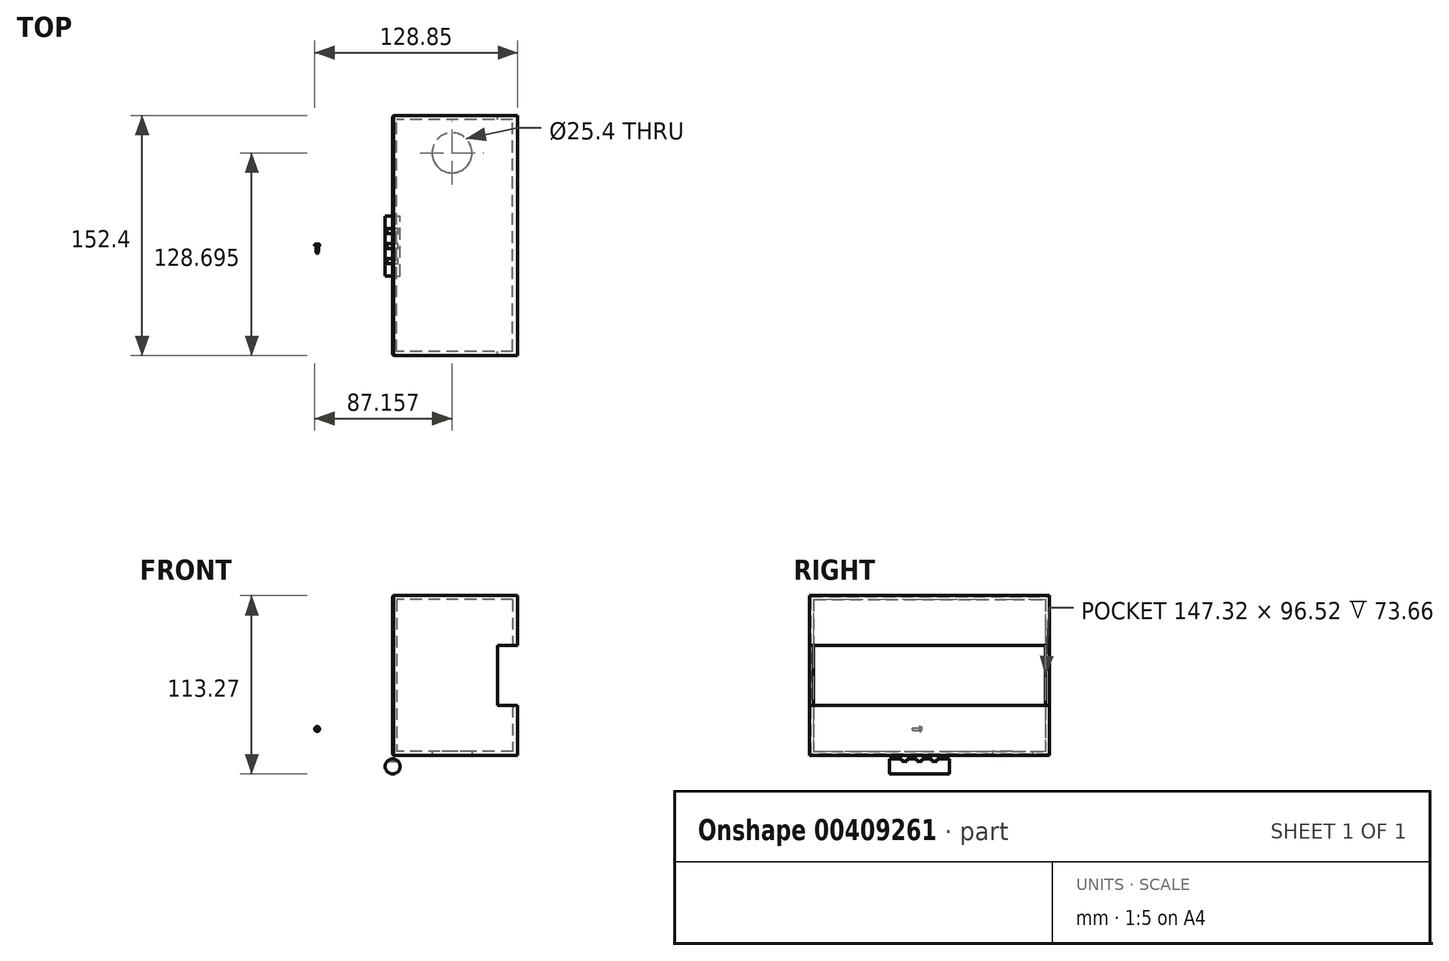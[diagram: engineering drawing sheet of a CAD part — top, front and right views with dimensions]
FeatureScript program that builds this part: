
annotation { "Feature Type Name" : "Feature", "Feature Type Description" : "" }
export const myFeature = defineFeature(function(context is Context, id is Id, definition is map)
    precondition{}
    {
        {
            var Q0;
            Q0=qCreatedBy(makeId("Front.planeOp"),FACE);
            var sketch = newSketch(context, id + "F0", { "sketchPlane" : qUnion([Q0])});
            skCircle(sketch, "E0", {"center": v(0, 0) * mm, "radius": 4.76 * mm});
            skSolve(sketch);
        }
        {
            var Q0;
            Q0=qSketchRegion(id+"F0",true);
            extrude(context, id + "F1", {"entities" : qUnion([Q0]), "endBound" : BoundingType.SYMMETRIC, "depth" : 38.1 * mm});
        }
        {
            var Q0;
            Q0=qCreatedBy(makeId("Right.planeOp"),FACE);
            var sketch = newSketch(context, id + "F2", { "sketchPlane" : qUnion([Q0])});
            skLineSegment(sketch, "E1.bottom", {"start": v(-1.59, 6.48) * mm, "end": v(1.59, 6.48) * mm});
            skLineSegment(sketch, "E1.top", {"start": v(-1.59, 3.18) * mm, "end": v(1.59, 3.18) * mm});
            skLineSegment(sketch, "E1.left", {"start": v(-1.59, 6.48) * mm, "end": v(-1.59, 3.18) * mm});
            skLineSegment(sketch, "E1.right", {"start": v(1.59, 6.48) * mm, "end": v(1.59, 3.18) * mm});
            skLineSegment(sketch, "E2.bottom", {"start": v(7.94, 6.48) * mm, "end": v(11.11, 6.48) * mm});
            skLineSegment(sketch, "E2.top", {"start": v(7.94, 3.17) * mm, "end": v(11.11, 3.18) * mm});
            skLineSegment(sketch, "E2.left", {"start": v(7.94, 6.48) * mm, "end": v(7.94, 3.17) * mm});
            skLineSegment(sketch, "E2.right", {"start": v(11.11, 6.48) * mm, "end": v(11.11, 3.18) * mm});
            skLineSegment(sketch, "E3.MirrorCS", {"start": v(-7.94, 6.48) * mm, "end": v(-11.11, 6.48) * mm});
            skLineSegment(sketch, "E4.MirrorCS", {"start": v(-11.11, 6.48) * mm, "end": v(-11.11, 3.18) * mm});
            skLineSegment(sketch, "E5.MirrorCS", {"start": v(-7.94, 3.17) * mm, "end": v(-11.11, 3.18) * mm});
            skLineSegment(sketch, "E6.MirrorCS", {"start": v(-7.94, 6.48) * mm, "end": v(-7.94, 3.17) * mm});
            skSolve(sketch);
        }
        {
            var Q0;
            Q0=qSketchRegion(id+"F2",true);
            extrude(context, id + "F3", {"entities" : qUnion([Q0]), "operationType" : NewBodyOperationType.REMOVE, "endBound" : BoundingType.SYMMETRIC, "oppositeDirection" : true, "depth" : 25.4 * mm});
        }
        {
            var Q0;
            Q0=qCreatedBy(makeId("Right.planeOp"),FACE);
            var sketch = newSketch(context, id + "F4", { "sketchPlane" : qUnion([Q0])});
            skLineSegment(sketch, "E7.bottom", {"start": v(-69.66, 108.51) * mm, "end": v(82.74, 108.51) * mm});
            skLineSegment(sketch, "E7.top", {"start": v(-69.66, 6.91) * mm, "end": v(82.74, 6.91) * mm});
            skLineSegment(sketch, "E7.left", {"start": v(-69.66, 108.51) * mm, "end": v(-69.66, 6.91) * mm});
            skLineSegment(sketch, "E7.right", {"start": v(82.74, 108.51) * mm, "end": v(82.74, 6.91) * mm});
            skSolve(sketch);
        }
        {
            var Q0;
            Q0=qSketchRegion(id+"F4",true);
            extrude(context, id + "F5", {"entities" : qUnion([Q0]), "depth" : 76.2 * mm});
        }
        {
            var Q0;
            Q0=makeQuery(id+"F5.opExtrude","CAP_FACE",FACE,{"disambiguationData":[OSD([sQuery(id+"F4.wireOp",EDGE,"E7.bottom"),sQuery(id+"F4.wireOp",EDGE,"E7.top"),sQuery(id+"F4.wireOp",EDGE,"E7.left"),sQuery(id+"F4.wireOp",EDGE,"E7.right")])],"isStart":false});
            shell(context, id + "F6", {"entities" : qUnion([Q0]), "thickness" : 2.54 * mm});
        }
        {
            var Q0;
            Q0=makeQuery(id+"F5.opExtrude","CAP_FACE",FACE,{"disambiguationData":[OSD([sQuery(id+"F4.wireOp",EDGE,"E7.bottom"),sQuery(id+"F4.wireOp",EDGE,"E7.top"),sQuery(id+"F4.wireOp",EDGE,"E7.left"),sQuery(id+"F4.wireOp",EDGE,"E7.right")])],"isStart":false});
            var sketch = newSketch(context, id + "F7", { "sketchPlane" : qUnion([Q0])});
            skLineSegment(sketch, "E8.bottom", {"start": v(-69.66, 108.51) * mm, "end": v(82.74, 108.51) * mm});
            skLineSegment(sketch, "E8.top", {"start": v(-69.66, 6.91) * mm, "end": v(82.74, 6.91) * mm});
            skLineSegment(sketch, "E8.left", {"start": v(-69.66, 108.51) * mm, "end": v(-69.66, 6.91) * mm});
            skLineSegment(sketch, "E8.right", {"start": v(82.74, 108.51) * mm, "end": v(82.74, 6.91) * mm});
            skSolve(sketch);
        }
        {
            var Q0;
            Q0=qSketchRegion(id+"F7",true);
            extrude(context, id + "F8", {"entities" : qUnion([Q0]), "operationType" : NewBodyOperationType.ADD, "depth" : 3.17 * mm});
        }
        {
            var Q0;
            Q0=makeQuery(id+"F8.opExtrude","CAP_FACE",FACE,{"disambiguationData":[OSD([sQuery(id+"F7.wireOp",EDGE,"E8.bottom"),sQuery(id+"F7.wireOp",EDGE,"E8.top"),sQuery(id+"F7.wireOp",EDGE,"E8.left"),sQuery(id+"F7.wireOp",EDGE,"E8.right")])],"isStart":false});
            var sketch = newSketch(context, id + "F9", { "sketchPlane" : qUnion([Q0])});
            skLineSegment(sketch, "E9.bottom", {"start": v(-82.06, 76.76) * mm, "end": v(95.74, 76.76) * mm});
            skLineSegment(sketch, "E9.top", {"start": v(-82.06, 38.66) * mm, "end": v(95.74, 38.66) * mm});
            skLineSegment(sketch, "E9.left", {"start": v(-82.06, 76.76) * mm, "end": v(-82.06, 38.66) * mm});
            skLineSegment(sketch, "E9.right", {"start": v(95.74, 76.76) * mm, "end": v(95.74, 38.66) * mm});
            skLineSegment(sketch, "E10", {"start": v(-69.66, 57.71) * mm, "end": v(82.74, 57.71) * mm, "construction": true});
            skSolve(sketch);
        }
        {
            var Q0;
            Q0=qSketchRegion(id+"F9",true);
            extrude(context, id + "F10", {"entities" : qUnion([Q0]), "operationType" : NewBodyOperationType.REMOVE, "oppositeDirection" : true, "depth" : 12.7 * mm});
        }
        {
            var Q0;
            Q0=makeQuery(id+"F8.boolean.opBoolean","MERGE",FACE,{"derivedFrom":[makeQuery(id+"F5.opExtrude","SWEPT_FACE",FACE,{"disambiguationData":[OSD([sQuery(id+"F4.wireOp",EDGE,"E7.top")])]}),makeQuery(id+"F8.opExtrude","SWEPT_FACE",FACE,{"disambiguationData":[OSD([sQuery(id+"F7.wireOp",EDGE,"E8.top")])]})]});
            var sketch = newSketch(context, id + "F11", { "sketchPlane" : qUnion([Q0])});
            skCircle(sketch, "E11", {"center": v(37.69, -59.03) * mm, "radius": 12.7 * mm});
            skSolve(sketch);
        }
        {
            var Q0;
            Q0=qSketchRegion(id+"F11",true);
            extrude(context, id + "F12", {"entities" : qUnion([Q0]), "operationType" : NewBodyOperationType.REMOVE, "oppositeDirection" : true, "depth" : 25.4 * mm});
        }
        {
            var Q0;
            Q0=qCreatedBy(makeId("Front.planeOp"),FACE);
            var sketch = newSketch(context, id + "F13", { "sketchPlane" : qUnion([Q0])});
            skCircle(sketch, "E12", {"center": v(-47.88, 23.8) * mm, "radius": 0.8 * mm});
            skSolve(sketch);
        }
        {
            var Q0;
            Q0=qSketchRegion(id+"F13",true);
            extrude(context, id + "F14", {"entities" : qUnion([Q0]), "depth" : 4.76 * mm});
        }
        {
            var Q0;
            Q0=makeQuery(id+"F14.opExtrude","CAP_EDGE",EDGE,{"disambiguationData":[OSD([sQuery(id+"F13.wireOp",EDGE,"E12")])],"isStart":false});
            var Q1;
            Q1=makeQuery(id+"F5.opExtrude","CAP_FACE",FACE,{"disambiguationData":[OSD([sQuery(id+"F4.wireOp",EDGE,"E7.bottom"),sQuery(id+"F4.wireOp",EDGE,"E7.top"),sQuery(id+"F4.wireOp",EDGE,"E7.left"),sQuery(id+"F4.wireOp",EDGE,"E7.right")])],"isStart":true});
            chamfer(context, id + "F15", {"entities" : qUnion([Q0, Q1]), "width" : 0.69 * mm, "tangentPropagation" : true});
        }
        {
            var Q0;
            Q0=makeQuery(id+"F14.opExtrude","CAP_FACE",FACE,{"disambiguationData":[OSD([sQuery(id+"F13.wireOp",EDGE,"E12")])],"isStart":true});
            var sketch = newSketch(context, id + "F16", { "sketchPlane" : qUnion([Q0])});
            skCircle(sketch, "E13", {"center": v(47.88, 23.8) * mm, "radius": 1.59 * mm});
            skSolve(sketch);
        }
        {
            var Q0;
            Q0=qSketchRegion(id+"F16",true);
            extrude(context, id + "F17", {"entities" : qUnion([Q0]), "operationType" : NewBodyOperationType.ADD, "depth" : 1.27 * mm});
        }
        {
            var Q0;
            Q0=makeQuery(id+"F17.opExtrude","CAP_EDGE",EDGE,{"disambiguationData":[OSD([sQuery(id+"F16.wireOp",EDGE,"E13")])],"isStart":false});
            fillet(context, id + "F18", {"entities" : qUnion([Q0]), "radius" : 0.76 * mm, "tangentPropagation" : true, "allowEdgeOverflow" : false});
        }
        {
            var Q0;
            Q0=makeQuery(id+"F17.opExtrude","CAP_FACE",FACE,{"disambiguationData":[OSD([sQuery(id+"F16.wireOp",EDGE,"E13")])],"isStart":false});
            var sketch = newSketch(context, id + "F19", { "sketchPlane" : qUnion([Q0])});
            skLineSegment(sketch, "E14.bottom", {"start": v(47.76, 24.36) * mm, "end": v(47.98, 24.36) * mm});
            skLineSegment(sketch, "E14.top", {"start": v(47.76, 23.19) * mm, "end": v(47.98, 23.19) * mm});
            skLineSegment(sketch, "E14.left", {"start": v(47.76, 24.36) * mm, "end": v(47.76, 23.19) * mm});
            skLineSegment(sketch, "E14.right", {"start": v(47.98, 24.36) * mm, "end": v(47.98, 23.19) * mm});
            skSolve(sketch);
        }
        {
            var Q0;
            Q0=qSketchRegion(id+"F19",true);
            extrude(context, id + "F20", {"entities" : qUnion([Q0]), "operationType" : NewBodyOperationType.REMOVE, "oppositeDirection" : true, "depth" : 0.76 * mm});
        }
        {
            var Q0;
            {var subQ0=sQuery(id+"F16.wireOp",EDGE,"E13");Q0=makeQuery(id+"F20.boolean.opBoolean","SPLIT",FACE,{"disambiguationData":[TD([makeQuery(id+"F20.opExtrude","SWEPT_FACE",FACE,{"disambiguationData":[OSD([sQuery(id+"F19.wireOp",EDGE,"E14.right")])]})])],"derivedFrom":makeQuery(id+"F17.opExtrude","CAP_FACE",FACE,{"disambiguationData":[OSD([subQ0])],"isStart":false})});}
            var sketch = newSketch(context, id + "F21", { "sketchPlane" : qUnion([Q0])});
            skLineSegment(sketch, "E15.bottom", {"start": v(47.45, 23.88) * mm, "end": v(48.3, 23.88) * mm});
            skLineSegment(sketch, "E15.top", {"start": v(47.45, 23.67) * mm, "end": v(48.3, 23.67) * mm});
            skLineSegment(sketch, "E15.left", {"start": v(47.45, 23.88) * mm, "end": v(47.45, 23.67) * mm});
            skLineSegment(sketch, "E15.right", {"start": v(48.3, 23.88) * mm, "end": v(48.3, 23.67) * mm});
            skSolve(sketch);
        }
        {
            var Q0;
            Q0=qSketchRegion(id+"F21",true);
            extrude(context, id + "F22", {"entities" : qUnion([Q0]), "operationType" : NewBodyOperationType.REMOVE, "oppositeDirection" : true, "depth" : 0.76 * mm});
        }
    });
